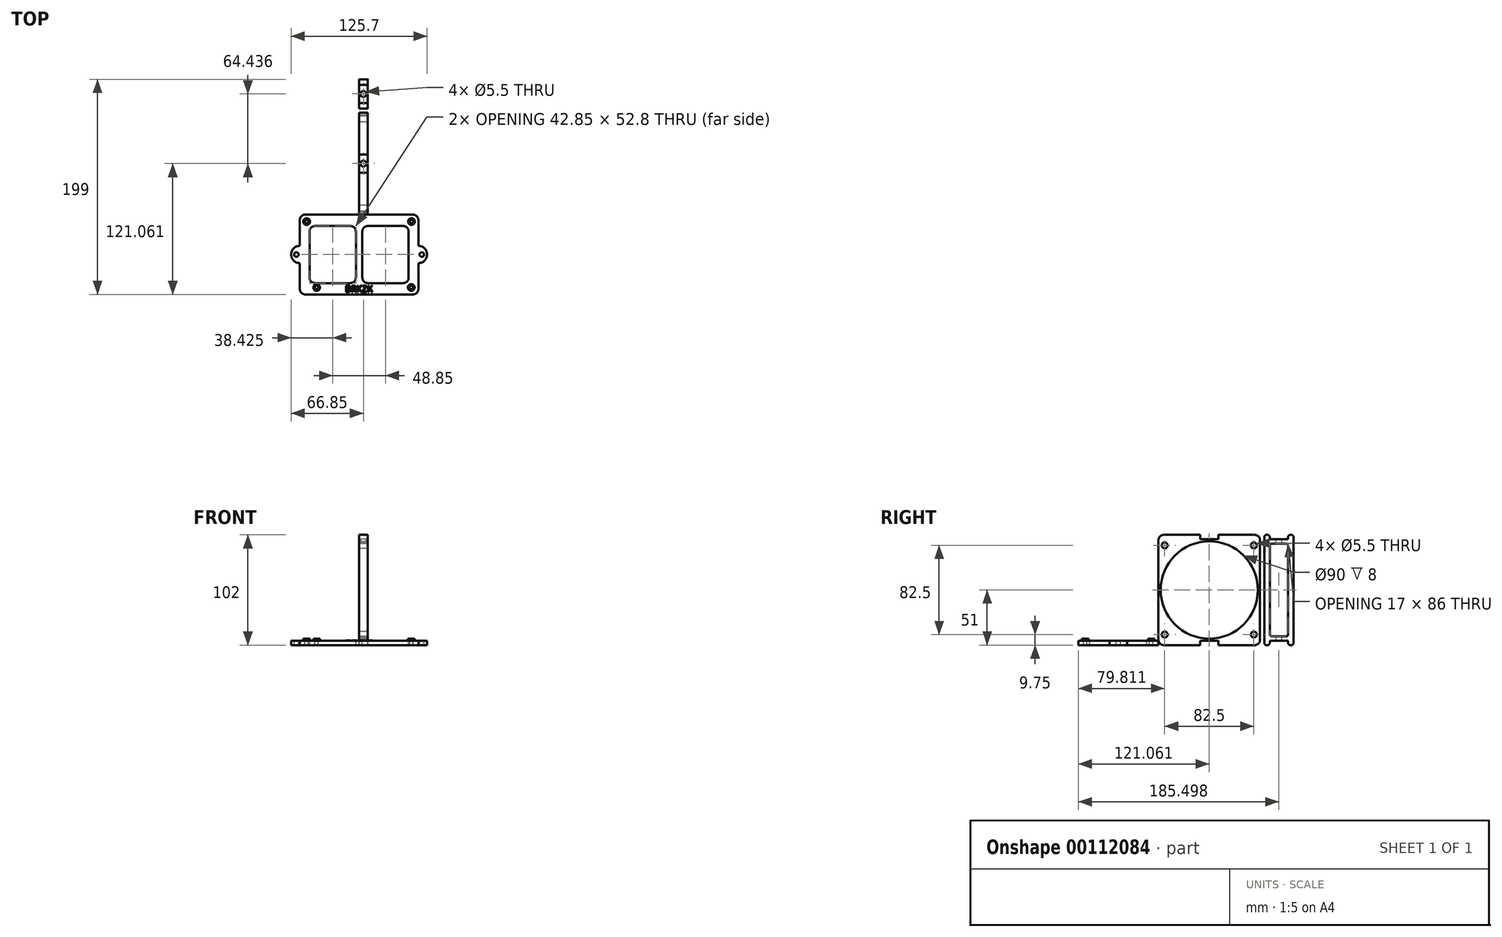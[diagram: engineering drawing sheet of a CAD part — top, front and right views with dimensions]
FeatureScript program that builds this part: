
annotation { "Feature Type Name" : "Feature", "Feature Type Description" : "" }
export const myFeature = defineFeature(function(context is Context, id is Id, definition is map)
    precondition{}
    {
        {
            assignVariable(context, id + "F0", {"name" : "hole_diameter", "anyValue" : 3.2 * mm});
        }
        {
            assignVariable(context, id + "F1", {"name" : "frame_z", "anyValue" : 4 * mm});
        }
        {
            assignVariable(context, id + "F2", {"name" : "hole_padding_z", "anyValue" : 2 * mm});
        }
        {
            var Q0;
            Q0=qCreatedBy(makeId("Top.planeOp"),FACE);
            var sketch = newSketch(context, id + "F3", { "sketchPlane" : qUnion([Q0])});
            skLineSegment(sketch, "E0.bottom", {"start": v(-51.85, 33.9) * mm, "end": v(51.85, 33.9) * mm});
            skLineSegment(sketch, "E0.top", {"start": v(-51.85, -33.9) * mm, "end": v(51.85, -33.9) * mm});
            skLineSegment(sketch, "E0.left", {"start": v(-51.85, 33.9) * mm, "end": v(-51.85, -33.9) * mm});
            skLineSegment(sketch, "E0.right", {"start": v(51.85, 33.9) * mm, "end": v(51.85, -33.9) * mm});
            skCircle(sketch, "E1", {"center": v(-48.55, 30.5) * mm, "radius": 1.6 * mm});
            skCircle(sketch, "E2", {"center": v(48.45, 30.5) * mm, "radius": 1.6 * mm});
            skCircle(sketch, "E3", {"center": v(48.25, -30.5) * mm, "radius": 1.6 * mm});
            skCircle(sketch, "E4", {"center": v(-39.25, -30.5) * mm, "radius": 1.6 * mm});
            skLineSegment(sketch, "E5", {"start": v(-48.55, 30.5) * mm, "end": v(-48.55, 33.9) * mm});
            skLineSegment(sketch, "E6.bottom", {"start": v(-54.85, 36.9) * mm, "end": v(54.85, 36.9) * mm});
            skLineSegment(sketch, "E6.top", {"start": v(-54.85, -36.9) * mm, "end": v(54.85, -36.9) * mm});
            skLineSegment(sketch, "E6.left", {"start": v(-54.85, 36.9) * mm, "end": v(-54.85, -36.9) * mm});
            skLineSegment(sketch, "E6.right", {"start": v(54.85, 36.9) * mm, "end": v(54.85, -36.9) * mm});
            skLineSegment(sketch, "E7.bottom", {"start": v(-45.85, 26.4) * mm, "end": v(-3, 26.4) * mm});
            skLineSegment(sketch, "E7.top", {"start": v(-45.85, -26.4) * mm, "end": v(-3, -26.4) * mm});
            skLineSegment(sketch, "E7.left", {"start": v(-45.85, 26.4) * mm, "end": v(-45.85, -26.4) * mm});
            skLineSegment(sketch, "E7.right", {"start": v(-3, 26.4) * mm, "end": v(-3, -26.4) * mm});
            skPoint(sketch, "E8", {"position": v(0, 33.9) * mm});
            skLineSegment(sketch, "E9.MirrorCS", {"start": v(45.85, 26.4) * mm, "end": v(3, 26.4) * mm});
            skLineSegment(sketch, "E10.MirrorCS", {"start": v(45.85, 26.4) * mm, "end": v(45.85, -26.4) * mm});
            skLineSegment(sketch, "E11.MirrorCS", {"start": v(45.85, -26.4) * mm, "end": v(3, -26.4) * mm});
            skLineSegment(sketch, "E12.MirrorCS", {"start": v(3, 26.4) * mm, "end": v(3, -26.4) * mm});
            skCircle(sketch, "E13", {"center": v(-48.55, 30.5) * mm, "radius": 3.1 * mm});
            skCircle(sketch, "E14", {"center": v(48.45, 30.5) * mm, "radius": 3.1 * mm});
            skCircle(sketch, "E15", {"center": v(48.25, -30.5) * mm, "radius": 3.1 * mm});
            skCircle(sketch, "E16", {"center": v(-39.25, -30.5) * mm, "radius": 3.1 * mm});
            skArc(sketch, "E17", {"start": v(54.85, -8) * mm, "mid": v(62.85, 0) * mm, "end": v(54.85, 8) * mm});
            skCircle(sketch, "E18", {"center": v(58.05, 0) * mm, "radius": 2.1 * mm});
            skPoint(sketch, "E19", {"position": v(-54.85, 8) * mm});
            skPoint(sketch, "E20", {"position": v(-54.85, -8) * mm});
            skArc(sketch, "E21", {"start": v(-54.85, 8) * mm, "mid": v(-62.85, 0) * mm, "end": v(-54.85, -8) * mm});
            skCircle(sketch, "E22", {"center": v(-58.05, 0) * mm, "radius": 2.1 * mm});
            skText(sketch, "E23", { "text": "BRKZK", "fontName": "OpenSans-Regular.ttf"});
            skLineSegment(sketch, "E24", {"start": v(-13.04, -28.65) * mm, "end": v(-13.04, -26.4) * mm});
            skLineSegment(sketch, "E25", {"start": v(-13.04, -34.65) * mm, "end": v(-13.04, -36.9) * mm});
            const initialGuessF3  = {"E23": [-0.01304, -0.03465, 1, 0, 0.006]};
            skSetInitialGuess(sketch, initialGuessF3);
            skSolve(sketch);
        }
        {
            var Q0;
            {var subQ1=sQuery(id+"F3.wireOp",EDGE,"E0.top");Q0=makeQuery(id+"F3.imprint","IMPRINT",FACE,{"disambiguationData":[TD([[makeQuery(id+"F3.imprint","IMPRINT",EDGE,{"derivedFrom":subQ1}),-1.0]])]});}
            var Q1;
            {var subQ1=sQuery(id+"F3.wireOp",EDGE,"E0.bottom");var subQ7=sQuery(id+"F3.wireOp",EDGE,"E0.left");var subQ8=makeQuery(id+"F3.imprint","INTERSECT",VERTEX,{"derivedFrom":[subQ1,subQ7]});Q1=makeQuery(id+"F3.imprint","IMPRINT",FACE,{"disambiguationData":[TD([[makeQuery(id+"F3.imprint","IMPRINT",EDGE,{"disambiguationData":[TD([[subQ8,-1.0]])],"derivedFrom":subQ1}),-1.0]])]});}
            var Q2;
            {var subQ1=sQuery(id+"F3.wireOp",EDGE,"E0.top");Q2=makeQuery(id+"F3.imprint","IMPRINT",FACE,{"disambiguationData":[TD([[makeQuery(id+"F3.imprint","IMPRINT",EDGE,{"derivedFrom":subQ1}),1.0]])]});}
            var Q3;
            Q3=makeQuery(id+"F3.imprint","IMPRINT",FACE,{"disambiguationData":[TD([[makeQuery(id+"F3.imprint","IMPRINT",EDGE,{"derivedFrom":sQuery(id+"F3.wireOp",EDGE,"E1")}),-1.0]])]});
            var Q4;
            Q4=makeQuery(id+"F3.imprint","IMPRINT",FACE,{"disambiguationData":[TD([[makeQuery(id+"F3.imprint","IMPRINT",EDGE,{"derivedFrom":sQuery(id+"F3.wireOp",EDGE,"E4")}),-1.0]])]});
            var Q5;
            Q5=makeQuery(id+"F3.imprint","IMPRINT",FACE,{"disambiguationData":[TD([[makeQuery(id+"F3.imprint","IMPRINT",EDGE,{"derivedFrom":sQuery(id+"F3.wireOp",EDGE,"E3")}),-1.0]])]});
            var Q6;
            Q6=makeQuery(id+"F3.imprint","IMPRINT",FACE,{"disambiguationData":[TD([[makeQuery(id+"F3.imprint","IMPRINT",EDGE,{"derivedFrom":sQuery(id+"F3.wireOp",EDGE,"E2")}),-1.0]])]});
            var Q7;
            {var subQ0=sQuery(id+"F3.wireOp",EDGE,"E17");Q7=makeQuery(id+"F3.imprint","IMPRINT",FACE,{"disambiguationData":[TD([[makeQuery(id+"F3.imprint","IMPRINT",EDGE,{"derivedFrom":subQ0}),1.0]])]});}
            var Q8;
            {var subQ0=sQuery(id+"F3.wireOp",EDGE,"E21");Q8=makeQuery(id+"F3.imprint","IMPRINT",FACE,{"disambiguationData":[TD([[makeQuery(id+"F3.imprint","IMPRINT",EDGE,{"derivedFrom":subQ0}),1.0]])]});}
            var Q9;
            Q9=makeQuery(id+"F3.imprint","IMPRINT",FACE,{"disambiguationData":[TD([[makeQuery(id+"F3.imprint","IMPRINT",EDGE,{"derivedFrom":sQuery(id+"F3.wireOp",EDGE,"c91511c5-1518-4a77-b889-c73128401ac6.sketch_text.stroke-11")}),1.0]])]});
            var Q10;
            Q10=makeQuery(id+"F3.imprint","IMPRINT",FACE,{"disambiguationData":[TD([[makeQuery(id+"F3.imprint","IMPRINT",EDGE,{"derivedFrom":sQuery(id+"F3.wireOp",EDGE,"c91511c5-1518-4a77-b889-c73128401ac6.sketch_text.stroke-18")}),1.0]])]});
            var Q11;
            Q11=makeQuery(id+"F3.imprint","IMPRINT",FACE,{"disambiguationData":[TD([[makeQuery(id+"F3.imprint","IMPRINT",EDGE,{"derivedFrom":sQuery(id+"F3.wireOp",EDGE,"c91511c5-1518-4a77-b889-c73128401ac6.sketch_text.stroke-36")}),1.0]])]});
            var Q12;
            Q12=makeQuery(id+"F3.imprint","IMPRINT",FACE,{"disambiguationData":[TD([[makeQuery(id+"F3.imprint","IMPRINT",EDGE,{"derivedFrom":sQuery(id+"F3.wireOp",EDGE,"c91511c5-1518-4a77-b889-c73128401ac6.sketch_text.stroke-0")}),-1.0]])]});
            var Q13;
            Q13=makeQuery(id+"F3.imprint","IMPRINT",FACE,{"disambiguationData":[TD([[makeQuery(id+"F3.imprint","IMPRINT",EDGE,{"derivedFrom":sQuery(id+"F3.wireOp",EDGE,"c91511c5-1518-4a77-b889-c73128401ac6.sketch_text.stroke-25")}),-1.0]])]});
            var Q14;
            Q14=makeQuery(id+"F3.imprint","IMPRINT",FACE,{"disambiguationData":[TD([[makeQuery(id+"F3.imprint","IMPRINT",EDGE,{"derivedFrom":sQuery(id+"F3.wireOp",EDGE,"c91511c5-1518-4a77-b889-c73128401ac6.sketch_text.stroke-43")}),-1.0]])]});
            var Q15;
            Q15=makeQuery(id+"F3.imprint","IMPRINT",FACE,{"disambiguationData":[TD([[makeQuery(id+"F3.imprint","IMPRINT",EDGE,{"derivedFrom":sQuery(id+"F3.wireOp",EDGE,"c91511c5-1518-4a77-b889-c73128401ac6.sketch_text.stroke-55")}),-1.0]])]});
            var Q16;
            Q16=makeQuery(id+"F3.imprint","IMPRINT",FACE,{"disambiguationData":[TD([[makeQuery(id+"F3.imprint","IMPRINT",EDGE,{"derivedFrom":sQuery(id+"F3.wireOp",EDGE,"c91511c5-1518-4a77-b889-c73128401ac6.sketch_text.stroke-65")}),-1.0]])]});
            var Q17;
            Q17=makeQuery(id+"F3.imprint","IMPRINT",FACE,{"disambiguationData":[TD([[makeQuery(id+"F3.imprint","IMPRINT",EDGE,{"derivedFrom":sQuery(id+"F3.wireOp",EDGE,"E23.sketch_text.stroke-11")}),1.0]])]});
            var Q18;
            Q18=makeQuery(id+"F3.imprint","IMPRINT",FACE,{"disambiguationData":[TD([[makeQuery(id+"F3.imprint","IMPRINT",EDGE,{"derivedFrom":sQuery(id+"F3.wireOp",EDGE,"E23.sketch_text.stroke-0")}),-1.0]])]});
            var Q19;
            Q19=makeQuery(id+"F3.imprint","IMPRINT",FACE,{"disambiguationData":[TD([[makeQuery(id+"F3.imprint","IMPRINT",EDGE,{"derivedFrom":sQuery(id+"F3.wireOp",EDGE,"E23.sketch_text.stroke-25")}),-1.0]])]});
            var Q20;
            Q20=makeQuery(id+"F3.imprint","IMPRINT",FACE,{"disambiguationData":[TD([[makeQuery(id+"F3.imprint","IMPRINT",EDGE,{"derivedFrom":sQuery(id+"F3.wireOp",EDGE,"E23.sketch_text.stroke-18")}),1.0]])]});
            var Q21;
            Q21=makeQuery(id+"F3.imprint","IMPRINT",FACE,{"disambiguationData":[TD([[makeQuery(id+"F3.imprint","IMPRINT",EDGE,{"derivedFrom":sQuery(id+"F3.wireOp",EDGE,"E23.sketch_text.stroke-36")}),1.0]])]});
            var Q22;
            Q22=makeQuery(id+"F3.imprint","IMPRINT",FACE,{"disambiguationData":[TD([[makeQuery(id+"F3.imprint","IMPRINT",EDGE,{"derivedFrom":sQuery(id+"F3.wireOp",EDGE,"E23.sketch_text.stroke-43")}),-1.0]])]});
            var Q23;
            Q23=makeQuery(id+"F3.imprint","IMPRINT",FACE,{"disambiguationData":[TD([[makeQuery(id+"F3.imprint","IMPRINT",EDGE,{"derivedFrom":sQuery(id+"F3.wireOp",EDGE,"E23.sketch_text.stroke-55")}),-1.0]])]});
            var Q24;
            Q24=makeQuery(id+"F3.imprint","IMPRINT",FACE,{"disambiguationData":[TD([[makeQuery(id+"F3.imprint","IMPRINT",EDGE,{"derivedFrom":sQuery(id+"F3.wireOp",EDGE,"E23.sketch_text.stroke-65")}),-1.0]])]});
            var Q25;
            {var subQ0=sQuery(id+"F3.wireOp",EDGE,"E23.sketch_text.stroke-8");Q25=makeQuery(id+"F3.imprint","IMPRINT",FACE,{"disambiguationData":[TD([[makeQuery(id+"F3.imprint","IMPRINT",EDGE,{"derivedFrom":subQ0}),-1.0]])]});}
            var Q26;
            {var subQ7=sQuery(id+"F3.wireOp",EDGE,"E23.sketch_text.stroke-28");Q26=makeQuery(id+"F3.imprint","IMPRINT",FACE,{"disambiguationData":[TD([[makeQuery(id+"F3.imprint","IMPRINT",EDGE,{"derivedFrom":subQ7}),-1.0]])]});}
            var Q27;
            {var subQ5=sQuery(id+"F3.wireOp",EDGE,"E23.sketch_text.stroke-35");Q27=makeQuery(id+"F3.imprint","IMPRINT",FACE,{"disambiguationData":[TD([[makeQuery(id+"F3.imprint","IMPRINT",EDGE,{"derivedFrom":subQ5}),1.0]])]});}
            var Q28;
            {var subQ5=sQuery(id+"F3.wireOp",EDGE,"E23.sketch_text.stroke-45");Q28=makeQuery(id+"F3.imprint","IMPRINT",FACE,{"disambiguationData":[TD([[makeQuery(id+"F3.imprint","IMPRINT",EDGE,{"derivedFrom":subQ5}),1.0]])]});}
            var Q29;
            {var subQ5=sQuery(id+"F3.wireOp",EDGE,"E23.sketch_text.stroke-47");Q29=makeQuery(id+"F3.imprint","IMPRINT",FACE,{"disambiguationData":[TD([[makeQuery(id+"F3.imprint","IMPRINT",EDGE,{"derivedFrom":subQ5}),-1.0]])]});}
            var Q30;
            {var subQ5=sQuery(id+"F3.wireOp",EDGE,"E23.sketch_text.stroke-33");Q30=makeQuery(id+"F3.imprint","IMPRINT",FACE,{"disambiguationData":[TD([[makeQuery(id+"F3.imprint","IMPRINT",EDGE,{"derivedFrom":subQ5}),-1.0]])]});}
            var Q31;
            {var subQ5=sQuery(id+"F3.wireOp",EDGE,"E23.sketch_text.stroke-58");Q31=makeQuery(id+"F3.imprint","IMPRINT",FACE,{"disambiguationData":[TD([[makeQuery(id+"F3.imprint","IMPRINT",EDGE,{"derivedFrom":subQ5}),-1.0]])]});}
            var Q32;
            {var subQ1=sQuery(id+"F3.wireOp",EDGE,"E23.sketch_text.stroke-67");Q32=makeQuery(id+"F3.imprint","IMPRINT",FACE,{"disambiguationData":[TD([[makeQuery(id+"F3.imprint","IMPRINT",EDGE,{"derivedFrom":subQ1}),-1.0]])]});}
            var Q33;
            {var subQ5=sQuery(id+"F3.wireOp",EDGE,"E23.sketch_text.stroke-67");Q33=makeQuery(id+"F3.imprint","IMPRINT",FACE,{"disambiguationData":[TD([[makeQuery(id+"F3.imprint","IMPRINT",EDGE,{"derivedFrom":subQ5}),1.0]])]});}
            var Q34;
            {var subQ5=sQuery(id+"F3.wireOp",EDGE,"E23.sketch_text.stroke-69");Q34=makeQuery(id+"F3.imprint","IMPRINT",FACE,{"disambiguationData":[TD([[makeQuery(id+"F3.imprint","IMPRINT",EDGE,{"derivedFrom":subQ5}),-1.0]])]});}
            var Q35;
            {var subQ0=sQuery(id+"F3.wireOp",EDGE,"E23.sketch_text.stroke-21");Q35=makeQuery(id+"F3.imprint","IMPRINT",FACE,{"disambiguationData":[TD([[makeQuery(id+"F3.imprint","IMPRINT",EDGE,{"derivedFrom":subQ0}),1.0]])]});}
            var Q36;
            {var subQ1=sQuery(id+"F3.wireOp",EDGE,"E23.sketch_text.stroke-45");Q36=makeQuery(id+"F3.imprint","IMPRINT",FACE,{"disambiguationData":[TD([[makeQuery(id+"F3.imprint","IMPRINT",EDGE,{"derivedFrom":subQ1}),-1.0]])]});}
            extrude(context, id + "F4", {"entities" : qUnion([Q0, Q1, Q2, Q3, Q4, Q5, Q6, Q7, Q8, Q9, Q10, Q11, Q12, Q13, Q14, Q15, Q16, Q17, Q18, Q19, Q20, Q21, Q22, Q23, Q24, Q25, Q26, Q27, Q28, Q29, Q30, Q31, Q32, Q33, Q34, Q35, Q36]), "oppositeDirection" : true, "depth" : getVariable(context, 'frame_z')});
        }
        {
            var Q0;
            Q0=makeQuery(id+"F3.imprint","IMPRINT",FACE,{"disambiguationData":[TD([[makeQuery(id+"F3.imprint","IMPRINT",EDGE,{"derivedFrom":sQuery(id+"F3.wireOp",EDGE,"E1")}),-1.0]])]});
            var Q1;
            Q1=makeQuery(id+"F3.imprint","IMPRINT",FACE,{"disambiguationData":[TD([[makeQuery(id+"F3.imprint","IMPRINT",EDGE,{"derivedFrom":sQuery(id+"F3.wireOp",EDGE,"E4")}),-1.0]])]});
            var Q2;
            Q2=makeQuery(id+"F3.imprint","IMPRINT",FACE,{"disambiguationData":[TD([[makeQuery(id+"F3.imprint","IMPRINT",EDGE,{"derivedFrom":sQuery(id+"F3.wireOp",EDGE,"E3")}),-1.0]])]});
            var Q3;
            Q3=makeQuery(id+"F3.imprint","IMPRINT",FACE,{"disambiguationData":[TD([[makeQuery(id+"F3.imprint","IMPRINT",EDGE,{"derivedFrom":sQuery(id+"F3.wireOp",EDGE,"E2")}),-1.0]])]});
            extrude(context, id + "F5", {"entities" : qUnion([Q0, Q1, Q2, Q3]), "operationType" : NewBodyOperationType.ADD, "depth" : getVariable(context, 'hole_padding_z')});
        }
        {
            var Q0;
            {var subQ1=sQuery(id+"F3.wireOp",EDGE,"E23.sketch_text.stroke-67");Q0=makeQuery(id+"F3.imprint","IMPRINT",FACE,{"disambiguationData":[TD([[makeQuery(id+"F3.imprint","IMPRINT",EDGE,{"derivedFrom":subQ1}),-1.0]])]});}
            var Q1;
            {var subQ6=sQuery(id+"F3.wireOp",EDGE,"E23.sketch_text.stroke-0");Q1=makeQuery(id+"F3.imprint","IMPRINT",FACE,{"disambiguationData":[TD([[makeQuery(id+"F3.imprint","IMPRINT",EDGE,{"derivedFrom":subQ6}),-1.0]])]});}
            var Q2;
            {var subQ0=sQuery(id+"F3.wireOp",EDGE,"E23.sketch_text.stroke-8");Q2=makeQuery(id+"F3.imprint","IMPRINT",FACE,{"disambiguationData":[TD([[makeQuery(id+"F3.imprint","IMPRINT",EDGE,{"derivedFrom":subQ0}),-1.0]])]});}
            var Q3;
            {var subQ7=sQuery(id+"F3.wireOp",EDGE,"E23.sketch_text.stroke-28");Q3=makeQuery(id+"F3.imprint","IMPRINT",FACE,{"disambiguationData":[TD([[makeQuery(id+"F3.imprint","IMPRINT",EDGE,{"derivedFrom":subQ7}),-1.0]])]});}
            var Q4;
            {var subQ5=sQuery(id+"F3.wireOp",EDGE,"E23.sketch_text.stroke-26");Q4=makeQuery(id+"F3.imprint","IMPRINT",FACE,{"disambiguationData":[TD([[makeQuery(id+"F3.imprint","IMPRINT",EDGE,{"derivedFrom":subQ5}),-1.0]])]});}
            var Q5;
            {var subQ5=sQuery(id+"F3.wireOp",EDGE,"E23.sketch_text.stroke-33");Q5=makeQuery(id+"F3.imprint","IMPRINT",FACE,{"disambiguationData":[TD([[makeQuery(id+"F3.imprint","IMPRINT",EDGE,{"derivedFrom":subQ5}),-1.0]])]});}
            var Q6;
            {var subQ1=sQuery(id+"F3.wireOp",EDGE,"E23.sketch_text.stroke-45");Q6=makeQuery(id+"F3.imprint","IMPRINT",FACE,{"disambiguationData":[TD([[makeQuery(id+"F3.imprint","IMPRINT",EDGE,{"derivedFrom":subQ1}),-1.0]])]});}
            var Q7;
            {var subQ5=sQuery(id+"F3.wireOp",EDGE,"E23.sketch_text.stroke-47");Q7=makeQuery(id+"F3.imprint","IMPRINT",FACE,{"disambiguationData":[TD([[makeQuery(id+"F3.imprint","IMPRINT",EDGE,{"derivedFrom":subQ5}),-1.0]])]});}
            var Q8;
            {var subQ5=sQuery(id+"F3.wireOp",EDGE,"E23.sketch_text.stroke-43");Q8=makeQuery(id+"F3.imprint","IMPRINT",FACE,{"disambiguationData":[TD([[makeQuery(id+"F3.imprint","IMPRINT",EDGE,{"derivedFrom":subQ5}),-1.0]])]});}
            var Q9;
            {var subQ5=sQuery(id+"F3.wireOp",EDGE,"E23.sketch_text.stroke-58");Q9=makeQuery(id+"F3.imprint","IMPRINT",FACE,{"disambiguationData":[TD([[makeQuery(id+"F3.imprint","IMPRINT",EDGE,{"derivedFrom":subQ5}),-1.0]])]});}
            var Q10;
            Q10=makeQuery(id+"F3.imprint","IMPRINT",FACE,{"disambiguationData":[TD([[makeQuery(id+"F3.imprint","IMPRINT",EDGE,{"derivedFrom":sQuery(id+"F3.wireOp",EDGE,"E23.sketch_text.stroke-55")}),-1.0]])]});
            var Q11;
            {var subQ5=sQuery(id+"F3.wireOp",EDGE,"E23.sketch_text.stroke-69");Q11=makeQuery(id+"F3.imprint","IMPRINT",FACE,{"disambiguationData":[TD([[makeQuery(id+"F3.imprint","IMPRINT",EDGE,{"derivedFrom":subQ5}),-1.0]])]});}
            var Q12;
            {var subQ5=sQuery(id+"F3.wireOp",EDGE,"E23.sketch_text.stroke-65");Q12=makeQuery(id+"F3.imprint","IMPRINT",FACE,{"disambiguationData":[TD([[makeQuery(id+"F3.imprint","IMPRINT",EDGE,{"derivedFrom":subQ5}),-1.0]])]});}
            extrude(context, id + "F6", {"entities" : qUnion([Q0, Q1, Q2, Q3, Q4, Q5, Q6, Q7, Q8, Q9, Q10, Q11, Q12]), "operationType" : NewBodyOperationType.ADD, "depth" : 0.4 * mm});
        }
        {
            var Q0;
            Q0=makeQuery(id+"F4.opExtrude","SWEPT_EDGE",EDGE,{"disambiguationData":[OSD([sQuery(id+"F3.wireOp",EDGE,"E6.top"),sQuery(id+"F3.wireOp",EDGE,"E6.left")])]});
            var Q1;
            Q1=makeQuery(id+"F4.opExtrude","SWEPT_EDGE",EDGE,{"disambiguationData":[OSD([sQuery(id+"F3.wireOp",EDGE,"E6.bottom"),sQuery(id+"F3.wireOp",EDGE,"E6.left")])]});
            var Q2;
            Q2=makeQuery(id+"F4.opExtrude","SWEPT_EDGE",EDGE,{"disambiguationData":[OSD([sQuery(id+"F3.wireOp",EDGE,"E6.top"),sQuery(id+"F3.wireOp",EDGE,"E6.right")])]});
            var Q3;
            Q3=makeQuery(id+"F4.opExtrude","SWEPT_EDGE",EDGE,{"disambiguationData":[OSD([sQuery(id+"F3.wireOp",EDGE,"E6.bottom"),sQuery(id+"F3.wireOp",EDGE,"E6.right")])]});
            fillet(context, id + "F7", {"entities" : qUnion([Q0, Q1, Q2, Q3]), "radius" : 5 * mm, "tangentPropagation" : true, "allowEdgeOverflow" : false});
        }
        {
            var Q0;
            Q0=makeQuery(id+"F4.opExtrude","SWEPT_EDGE",EDGE,{"disambiguationData":[OSD([sQuery(id+"F3.wireOp",EDGE,"E7.bottom"),sQuery(id+"F3.wireOp",EDGE,"E7.left")])]});
            var Q1;
            Q1=makeQuery(id+"F4.opExtrude","SWEPT_EDGE",EDGE,{"disambiguationData":[OSD([sQuery(id+"F3.wireOp",EDGE,"E9.MirrorCS"),sQuery(id+"F3.wireOp",EDGE,"E10.MirrorCS")])]});
            var Q2;
            Q2=makeQuery(id+"F4.opExtrude","SWEPT_EDGE",EDGE,{"disambiguationData":[OSD([sQuery(id+"F3.wireOp",EDGE,"E7.top"),sQuery(id+"F3.wireOp",EDGE,"E7.left")])]});
            var Q3;
            Q3=makeQuery(id+"F4.opExtrude","SWEPT_EDGE",EDGE,{"disambiguationData":[OSD([sQuery(id+"F3.wireOp",EDGE,"E10.MirrorCS"),sQuery(id+"F3.wireOp",EDGE,"E11.MirrorCS")])]});
            var Q4;
            Q4=makeQuery(id+"F4.opExtrude","SWEPT_EDGE",EDGE,{"disambiguationData":[OSD([sQuery(id+"F3.wireOp",EDGE,"E9.MirrorCS"),sQuery(id+"F3.wireOp",EDGE,"E12.MirrorCS")])]});
            var Q5;
            Q5=makeQuery(id+"F4.opExtrude","SWEPT_EDGE",EDGE,{"disambiguationData":[OSD([sQuery(id+"F3.wireOp",EDGE,"E7.bottom"),sQuery(id+"F3.wireOp",EDGE,"E7.right")])]});
            var Q6;
            Q6=makeQuery(id+"F4.opExtrude","SWEPT_EDGE",EDGE,{"disambiguationData":[OSD([sQuery(id+"F3.wireOp",EDGE,"E7.top"),sQuery(id+"F3.wireOp",EDGE,"E7.right")])]});
            var Q7;
            Q7=makeQuery(id+"F4.opExtrude","SWEPT_EDGE",EDGE,{"disambiguationData":[OSD([sQuery(id+"F3.wireOp",EDGE,"E11.MirrorCS"),sQuery(id+"F3.wireOp",EDGE,"E12.MirrorCS")])]});
            fillet(context, id + "F8", {"entities" : qUnion([Q0, Q1, Q2, Q3, Q4, Q5, Q6, Q7]), "radius" : 5 * mm, "tangentPropagation" : true, "allowEdgeOverflow" : false});
        }
        {
            assignVariable(context, id + "F9", {"name" : "hole_diameter", "anyValue" : 5.5 * mm});
        }
        {
            var Q0;
            Q0=qCreatedBy(makeId("Right.planeOp"),FACE);
            var sketch = newSketch(context, id + "F10", { "sketchPlane" : qUnion([Q0])});
            skLineSegment(sketch, "E26.bottom", {"start": v(37.16, 94) * mm, "end": v(131.16, 94) * mm});
            skLineSegment(sketch, "E26.top", {"start": v(37.16, 0) * mm, "end": v(131.16, 0) * mm});
            skLineSegment(sketch, "E26.left", {"start": v(37.16, 94) * mm, "end": v(37.16, 0) * mm});
            skLineSegment(sketch, "E26.right", {"start": v(131.16, 94) * mm, "end": v(131.16, 0) * mm});
            skCircle(sketch, "E27", {"center": v(42.91, 5.75) * mm, "radius": 2.75 * mm});
            skCircle(sketch, "E28", {"center": v(125.41, 5.75) * mm, "radius": 2.75 * mm});
            skLineSegment(sketch, "E29", {"start": v(42.91, 5.75) * mm, "end": v(37.16, 5.75) * mm});
            skLineSegment(sketch, "E30", {"start": v(125.41, 5.75) * mm, "end": v(131.16, 5.75) * mm});
            skCircle(sketch, "E31", {"center": v(42.91, 88.25) * mm, "radius": 2.75 * mm});
            skCircle(sketch, "E32", {"center": v(125.41, 88.25) * mm, "radius": 2.75 * mm});
            skLineSegment(sketch, "E33", {"start": v(42.91, 5.75) * mm, "end": v(42.91, 0) * mm});
            skLineSegment(sketch, "E34", {"start": v(42.91, 88.25) * mm, "end": v(42.91, 94) * mm});
            skCircle(sketch, "E35", {"center": v(84.16, 47) * mm, "radius": 45 * mm});
            skPoint(sketch, "E35.centerSnap0", {"position": v(84.16, 0) * mm});
            skPoint(sketch, "E35.centerSnap1", {"position": v(37.16, 47) * mm});
            skLineSegment(sketch, "E36.top", {"start": v(37.16, -4) * mm, "end": v(75.66, -4) * mm});
            skLineSegment(sketch, "E36.left", {"start": v(37.16, 0) * mm, "end": v(37.16, -4) * mm});
            skLineSegment(sketch, "E36.right", {"start": v(131.16, 0) * mm, "end": v(131.16, -4) * mm});
            skLineSegment(sketch, "E37", {"start": v(75.66, -4) * mm, "end": v(75.66, 0) * mm});
            skLineSegment(sketch, "E38", {"start": v(92.66, -4) * mm, "end": v(92.66, 0) * mm});
            skLineSegment(sketch, "E39.trimOffspring", {"start": v(92.66, -4) * mm, "end": v(131.16, -4) * mm});
            skLineSegment(sketch, "E40", {"start": v(75.66, -4) * mm, "end": v(92.66, -4) * mm});
            skLineSegment(sketch, "E41", {"start": v(75.66, 0) * mm, "end": v(75.66, 2.81) * mm});
            skLineSegment(sketch, "E42", {"start": v(92.66, 0) * mm, "end": v(92.66, 2.81) * mm});
            skLineSegment(sketch, "E43.top", {"start": v(37.16, 98) * mm, "end": v(131.16, 98) * mm});
            skLineSegment(sketch, "E43.left", {"start": v(37.16, 94) * mm, "end": v(37.16, 98) * mm});
            skLineSegment(sketch, "E43.right", {"start": v(131.16, 94) * mm, "end": v(131.16, 98) * mm});
            skLineSegment(sketch, "E44", {"start": v(75.66, 94) * mm, "end": v(75.66, 98) * mm});
            skPoint(sketch, "E44.endSnap0", {"position": v(84.16, 98) * mm});
            skLineSegment(sketch, "E45", {"start": v(92.66, 94) * mm, "end": v(92.66, 98) * mm});
            skLineSegment(sketch, "E46", {"start": v(75.66, 94) * mm, "end": v(75.66, 91.19) * mm});
            skLineSegment(sketch, "E47", {"start": v(92.66, 94) * mm, "end": v(92.66, 91.19) * mm});
            skSolve(sketch);
        }
        {
            var Q0;
            Q0=makeQuery(id+"F10.imprint","IMPRINT",FACE,{"disambiguationData":[TD([[makeQuery(id+"F10.imprint","IMPRINT",EDGE,{"derivedFrom":sQuery(id+"F10.wireOp",EDGE,"E28")}),-1.0]])]});
            var Q1;
            {var subQ5=sQuery(id+"F10.wireOp",EDGE,"E26.left");var subQ6=sQuery(id+"F10.wireOp",EDGE,"E26.top");var subQ7=makeQuery(id+"F10.imprint","INTERSECT",VERTEX,{"derivedFrom":[subQ6,subQ5]});Q1=makeQuery(id+"F10.imprint","IMPRINT",FACE,{"disambiguationData":[TD([[makeQuery(id+"F10.imprint","IMPRINT",EDGE,{"disambiguationData":[TD([[subQ7,-1.0]])],"derivedFrom":subQ6}),1.0]])]});}
            var Q2;
            {var subQ3=sQuery(id+"F10.wireOp",EDGE,"E27");var subQ7=sQuery(id+"F10.wireOp",EDGE,"E29");var subQ9=makeQuery(id+"F10.imprint","INTERSECT",VERTEX,{"derivedFrom":[subQ3,subQ7]});Q2=makeQuery(id+"F10.imprint","IMPRINT",FACE,{"disambiguationData":[TD([[makeQuery(id+"F10.imprint","IMPRINT",EDGE,{"disambiguationData":[TD([[subQ9,-1.0]])],"derivedFrom":subQ3}),-1.0]])]});}
            var Q3;
            Q3=makeQuery(id+"F10.imprint","IMPRINT",FACE,{"disambiguationData":[TD([[makeQuery(id+"F10.imprint","IMPRINT",EDGE,{"derivedFrom":sQuery(id+"F10.wireOp",EDGE,"E36.top")}),1.0]])]});
            var Q4;
            {var subQ0=sQuery(id+"F10.wireOp",EDGE,"E36.right");Q4=makeQuery(id+"F10.imprint","IMPRINT",FACE,{"disambiguationData":[TD([[makeQuery(id+"F10.imprint","IMPRINT",EDGE,{"derivedFrom":subQ0}),-1.0]])]});}
            var Q5;
            {var subQ0=sQuery(id+"F10.wireOp",EDGE,"E41");Q5=makeQuery(id+"F10.imprint","IMPRINT",FACE,{"disambiguationData":[TD([[makeQuery(id+"F10.imprint","IMPRINT",EDGE,{"derivedFrom":subQ0}),-1.0]])]});}
            var Q6;
            {var subQ0=sQuery(id+"F10.wireOp",EDGE,"E46");Q6=makeQuery(id+"F10.imprint","IMPRINT",FACE,{"disambiguationData":[TD([[makeQuery(id+"F10.imprint","IMPRINT",EDGE,{"derivedFrom":subQ0}),1.0]])]});}
            var Q7;
            {var subQ0=sQuery(id+"F10.wireOp",EDGE,"E43.right");Q7=makeQuery(id+"F10.imprint","IMPRINT",FACE,{"disambiguationData":[TD([[makeQuery(id+"F10.imprint","IMPRINT",EDGE,{"derivedFrom":subQ0}),1.0]])]});}
            var Q8;
            {var subQ0=sQuery(id+"F10.wireOp",EDGE,"E43.left");Q8=makeQuery(id+"F10.imprint","IMPRINT",FACE,{"disambiguationData":[TD([[makeQuery(id+"F10.imprint","IMPRINT",EDGE,{"derivedFrom":subQ0}),-1.0]])]});}
            var Q9;
            Q9=makeQuery(id+"F10.imprint","IMPRINT",FACE,{"disambiguationData":[TD([[makeQuery(id+"F10.imprint","IMPRINT",EDGE,{"derivedFrom":sQuery(id+"F10.wireOp",EDGE,"E31")}),-1.0]])]});
            extrude(context, id + "F11", {"entities" : qUnion([Q0, Q1, Q2, Q3, Q4, Q5, Q6, Q7, Q8, Q9]), "depth" : 8 * mm});
        }
        {
            var Q0;
            Q0=makeQuery(id+"F11.opExtrude","SWEPT_FACE",FACE,{"disambiguationData":[OSD([sQuery(id+"F10.wireOp",EDGE,"E26.top")])]});
            var sketch = newSketch(context, id + "F12", { "sketchPlane" : qUnion([Q0])});
            skPoint(sketch, "E48", {"position": v(4, -84.16) * mm});
            skPoint(sketch, "E48.positionSnap0", {"position": v(4, -75.66) * mm});
            skPoint(sketch, "E48.positionSnap1", {"position": v(8, -84.16) * mm});
            skSolve(sketch);
        }
        {
            var Q0;
            Q0=sQuery(id+"F12.wireOp",VERTEX,"E48");
            var Q1;
            Q1=makeQuery(id+"F11.opExtrude","SWEPT_BODY",BODY,{"disambiguationData":[OSD([sQuery(id+"F10.wireOp",EDGE,"E26.bottom"),sQuery(id+"F10.wireOp",EDGE,"E26.left"),sQuery(id+"F10.wireOp",EDGE,"E26.right"),sQuery(id+"F10.wireOp",EDGE,"E27"),sQuery(id+"F10.wireOp",EDGE,"E28"),sQuery(id+"F10.wireOp",EDGE,"E31"),sQuery(id+"F10.wireOp",EDGE,"E32"),sQuery(id+"F10.wireOp",EDGE,"E35"),sQuery(id+"F10.wireOp",EDGE,"E26.top"),sQuery(id+"F10.wireOp",EDGE,"E36.top"),sQuery(id+"F10.wireOp",EDGE,"E36.left"),sQuery(id+"F10.wireOp",EDGE,"E36.right"),sQuery(id+"F10.wireOp",EDGE,"E37"),sQuery(id+"F10.wireOp",EDGE,"E38"),sQuery(id+"F10.wireOp",EDGE,"E39.trimOffspring")])]});
            hole(context, id + "F13", {"style" : HoleStyle.SIMPLE, "endStyle" : HoleEndStyle.THROUGH, "holeDiameter" : getVariable(context, 'hole_diameter'), "isTappedThrough" : true, "tappedDepth" : 12 * mm, "tapClearance" : 3, "locations" : qUnion([Q0]), "scope" : qUnion([Q1])});
        }
        {
            var Q0;
            Q0=makeQuery(id+"F11.opExtrude","SWEPT_EDGE",EDGE,{"disambiguationData":[OSD([sQuery(id+"F10.wireOp",EDGE,"E43.top"),sQuery(id+"F10.wireOp",EDGE,"E43.right")])]});
            var Q1;
            Q1=makeQuery(id+"F11.opExtrude","SWEPT_EDGE",EDGE,{"disambiguationData":[OSD([sQuery(id+"F10.wireOp",EDGE,"E43.top"),sQuery(id+"F10.wireOp",EDGE,"E43.left")])]});
            var Q2;
            Q2=makeQuery(id+"F11.opExtrude","SWEPT_EDGE",EDGE,{"disambiguationData":[OSD([sQuery(id+"F10.wireOp",EDGE,"E36.right"),sQuery(id+"F10.wireOp",EDGE,"E39.trimOffspring")])]});
            var Q3;
            Q3=makeQuery(id+"F11.opExtrude","SWEPT_EDGE",EDGE,{"disambiguationData":[OSD([sQuery(id+"F10.wireOp",EDGE,"E36.top"),sQuery(id+"F10.wireOp",EDGE,"E36.left")])]});
            fillet(context, id + "F14", {"entities" : qUnion([Q0, Q1, Q2, Q3]), "radius" : 5 * mm, "tangentPropagation" : true, "allowEdgeOverflow" : false});
        }
        {
            var Q0;
            Q0=qCreatedBy(makeId("Right.planeOp"),FACE);
            var sketch = newSketch(context, id + "F15", { "sketchPlane" : qUnion([Q0])});
            skLineSegment(sketch, "E49.bottom", {"start": v(140.1, 0) * mm, "end": v(157.1, 0) * mm});
            skLineSegment(sketch, "E49.top", {"start": v(140.1, 94) * mm, "end": v(157.1, 94) * mm});
            skLineSegment(sketch, "E49.left", {"start": v(140.1, 0) * mm, "end": v(140.1, 94) * mm});
            skLineSegment(sketch, "E49.right", {"start": v(157.1, 0) * mm, "end": v(157.1, 94) * mm});
            skLineSegment(sketch, "E50", {"start": v(140.1, 0) * mm, "end": v(140.1, -4) * mm});
            skLineSegment(sketch, "E51", {"start": v(140.1, -4) * mm, "end": v(135.1, -4) * mm});
            skLineSegment(sketch, "E52", {"start": v(135.1, -4) * mm, "end": v(135.1, 98) * mm});
            skLineSegment(sketch, "E53", {"start": v(135.1, 98) * mm, "end": v(140.1, 98) * mm});
            skLineSegment(sketch, "E54", {"start": v(140.1, 98) * mm, "end": v(140.1, 94) * mm});
            skLineSegment(sketch, "E55.bottom", {"start": v(157.1, 98) * mm, "end": v(162.1, 98) * mm});
            skLineSegment(sketch, "E55.top", {"start": v(157.1, -4) * mm, "end": v(162.1, -4) * mm});
            skLineSegment(sketch, "E55.left", {"start": v(157.1, 98) * mm, "end": v(157.1, -4) * mm});
            skLineSegment(sketch, "E55.right", {"start": v(162.1, 98) * mm, "end": v(162.1, -4) * mm});
            skLineSegment(sketch, "E56", {"start": v(140.1, 90) * mm, "end": v(157.1, 90) * mm});
            skLineSegment(sketch, "E57", {"start": v(140.1, 4) * mm, "end": v(157.1, 4) * mm});
            skSolve(sketch);
        }
        {
            var Q0;
            {var subQ3=sQuery(id+"F15.wireOp",EDGE,"E55.bottom");Q0=makeQuery(id+"F15.imprint","IMPRINT",FACE,{"disambiguationData":[TD([[makeQuery(id+"F15.imprint","IMPRINT",EDGE,{"derivedFrom":subQ3}),-1.0]])]});}
            var Q1;
            {var subQ0=sQuery(id+"F15.wireOp",EDGE,"E49.bottom");Q1=makeQuery(id+"F15.imprint","IMPRINT",FACE,{"disambiguationData":[TD([[makeQuery(id+"F15.imprint","IMPRINT",EDGE,{"derivedFrom":subQ0}),1.0]])]});}
            var Q2;
            Q2=makeQuery(id+"F15.imprint","IMPRINT",FACE,{"disambiguationData":[TD([[makeQuery(id+"F15.imprint","IMPRINT",EDGE,{"derivedFrom":sQuery(id+"F15.wireOp",EDGE,"E49.left")}),1.0]])]});
            var Q3;
            {var subQ0=sQuery(id+"F15.wireOp",EDGE,"E49.top");Q3=makeQuery(id+"F15.imprint","IMPRINT",FACE,{"disambiguationData":[TD([[makeQuery(id+"F15.imprint","IMPRINT",EDGE,{"derivedFrom":subQ0}),-1.0]])]});}
            extrude(context, id + "F16", {"entities" : qUnion([Q0, Q1, Q2, Q3]), "depth" : 8 * mm});
        }
        {
            var Q0;
            Q0=makeQuery(id+"F16.opExtrude","SWEPT_FACE",FACE,{"disambiguationData":[OSD([sQuery(id+"F15.wireOp",EDGE,"E49.top")])]});
            var sketch = newSketch(context, id + "F17", { "sketchPlane" : qUnion([Q0])});
            skPoint(sketch, "E58", {"position": v(4, 148.6) * mm});
            skPoint(sketch, "E58.positionSnap0", {"position": v(4, 157.1) * mm});
            skPoint(sketch, "E58.positionSnap1", {"position": v(8, 148.6) * mm});
            skSolve(sketch);
        }
        {
            var Q0;
            Q0=sQuery(id+"F17.wireOp",VERTEX,"E58");
            var Q1;
            Q1=makeQuery(id+"F16.opExtrude","SWEPT_BODY",BODY,{"disambiguationData":[OSD([sQuery(id+"F15.wireOp",EDGE,"E49.bottom"),sQuery(id+"F15.wireOp",EDGE,"E49.top"),sQuery(id+"F15.wireOp",EDGE,"E49.left"),sQuery(id+"F15.wireOp",EDGE,"E50"),sQuery(id+"F15.wireOp",EDGE,"E51"),sQuery(id+"F15.wireOp",EDGE,"E52"),sQuery(id+"F15.wireOp",EDGE,"E53"),sQuery(id+"F15.wireOp",EDGE,"E54"),sQuery(id+"F15.wireOp",EDGE,"E55.bottom"),sQuery(id+"F15.wireOp",EDGE,"E55.top"),sQuery(id+"F15.wireOp",EDGE,"E55.left"),sQuery(id+"F15.wireOp",EDGE,"E55.right"),sQuery(id+"F15.wireOp",EDGE,"E56"),sQuery(id+"F15.wireOp",EDGE,"E57")])]});
            hole(context, id + "F18", {"style" : HoleStyle.SIMPLE, "endStyle" : HoleEndStyle.THROUGH, "holeDiameter" : getVariable(context, 'hole_diameter'), "isTappedThrough" : true, "tappedDepth" : 12 * mm, "tapClearance" : 3, "locations" : qUnion([Q0]), "scope" : qUnion([Q1])});
        }
        {
            var Q0;
            Q0=makeQuery(id+"F16.opExtrude","SWEPT_EDGE",EDGE,{"disambiguationData":[OSD([sQuery(id+"F15.wireOp",EDGE,"E51"),sQuery(id+"F15.wireOp",EDGE,"E52")])]});
            var Q1;
            Q1=makeQuery(id+"F16.opExtrude","SWEPT_EDGE",EDGE,{"disambiguationData":[OSD([sQuery(id+"F15.wireOp",EDGE,"E50"),sQuery(id+"F15.wireOp",EDGE,"E51")])]});
            var Q2;
            Q2=makeQuery(id+"F16.opExtrude","SWEPT_EDGE",EDGE,{"disambiguationData":[OSD([sQuery(id+"F15.wireOp",EDGE,"E55.top"),sQuery(id+"F15.wireOp",EDGE,"E55.left")])]});
            var Q3;
            Q3=makeQuery(id+"F16.opExtrude","SWEPT_EDGE",EDGE,{"disambiguationData":[OSD([sQuery(id+"F15.wireOp",EDGE,"E55.top"),sQuery(id+"F15.wireOp",EDGE,"E55.right")])]});
            var Q4;
            Q4=makeQuery(id+"F16.opExtrude","SWEPT_EDGE",EDGE,{"disambiguationData":[OSD([sQuery(id+"F15.wireOp",EDGE,"E55.bottom"),sQuery(id+"F15.wireOp",EDGE,"E55.right")])]});
            var Q5;
            Q5=makeQuery(id+"F16.opExtrude","SWEPT_EDGE",EDGE,{"disambiguationData":[OSD([sQuery(id+"F15.wireOp",EDGE,"E55.bottom"),sQuery(id+"F15.wireOp",EDGE,"E55.left")])]});
            var Q6;
            Q6=makeQuery(id+"F16.opExtrude","SWEPT_EDGE",EDGE,{"disambiguationData":[OSD([sQuery(id+"F15.wireOp",EDGE,"E53"),sQuery(id+"F15.wireOp",EDGE,"E54")])]});
            var Q7;
            Q7=makeQuery(id+"F16.opExtrude","SWEPT_EDGE",EDGE,{"disambiguationData":[OSD([sQuery(id+"F15.wireOp",EDGE,"E52"),sQuery(id+"F15.wireOp",EDGE,"E53")])]});
            var Q8;
            Q8=makeQuery(id+"F16.opExtrude","SWEPT_EDGE",EDGE,{"disambiguationData":[OSD([sQuery(id+"F15.wireOp",EDGE,"E49.left"),sQuery(id+"F15.wireOp",EDGE,"E56")])]});
            var Q9;
            Q9=makeQuery(id+"F16.opExtrude","SWEPT_EDGE",EDGE,{"disambiguationData":[OSD([sQuery(id+"F15.wireOp",EDGE,"E55.left"),sQuery(id+"F15.wireOp",EDGE,"E56")])]});
            var Q10;
            Q10=makeQuery(id+"F16.opExtrude","SWEPT_EDGE",EDGE,{"disambiguationData":[OSD([sQuery(id+"F15.wireOp",EDGE,"E49.left"),sQuery(id+"F15.wireOp",EDGE,"E57")])]});
            var Q11;
            Q11=makeQuery(id+"F16.opExtrude","SWEPT_EDGE",EDGE,{"disambiguationData":[OSD([sQuery(id+"F15.wireOp",EDGE,"E55.left"),sQuery(id+"F15.wireOp",EDGE,"E57")])]});
            fillet(context, id + "F19", {"entities" : qUnion([Q0, Q1, Q2, Q3, Q4, Q5, Q6, Q7, Q8, Q9, Q10, Q11]), "radius" : 2 * mm, "tangentPropagation" : true, "allowEdgeOverflow" : false});
        }
    });
